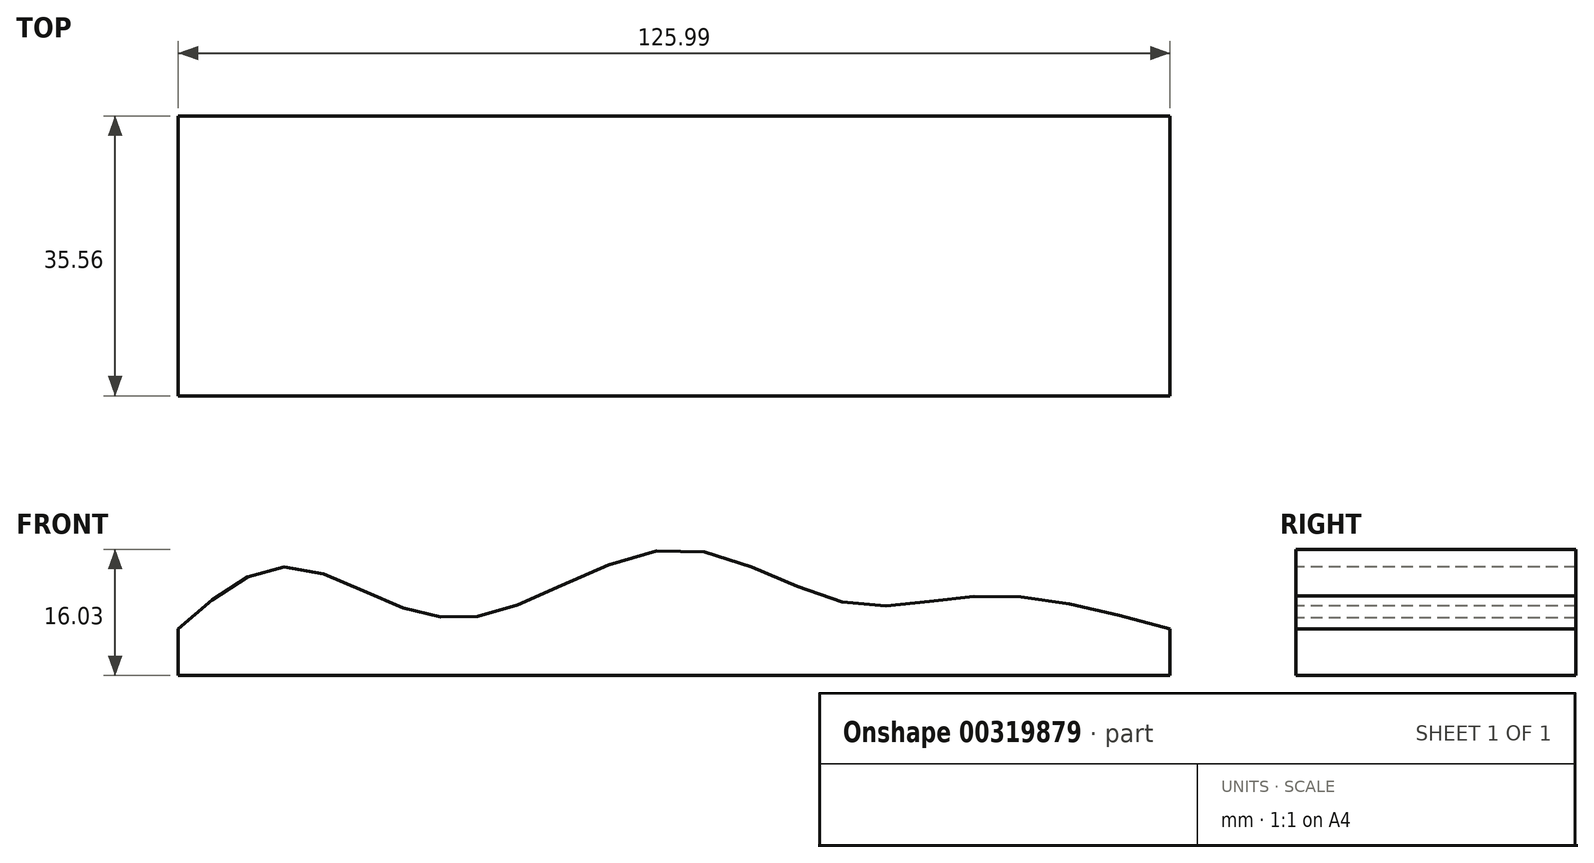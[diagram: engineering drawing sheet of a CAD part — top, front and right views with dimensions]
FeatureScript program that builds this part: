
annotation { "Feature Type Name" : "Feature", "Feature Type Description" : "" }
export const myFeature = defineFeature(function(context is Context, id is Id, definition is map)
    precondition{}
    {
        {
            var Q0;
            Q0=qCreatedBy(makeId("Front.planeOp"),FACE);
            var sketch = newSketch(context, id + "F0", { "sketchPlane" : qUnion([Q0])});
            skLineSegment(sketch, "E0.bottom", {"start": v(-134.15, -27.42) * mm, "end": v(-8.16, -27.42) * mm});
            skLineSegment(sketch, "E0.top", {"start": v(-134.15, -21.51) * mm, "end": v(-8.16, -21.51) * mm});
            skLineSegment(sketch, "E0.left", {"start": v(-134.15, -27.42) * mm, "end": v(-134.15, -21.51) * mm});
            skLineSegment(sketch, "E0.right", {"start": v(-8.16, -27.42) * mm, "end": v(-8.16, -21.51) * mm});
            skFitSpline(sketch, "E1", {"points": [v(-134.15, -21.51) * mm, v(-120.65, -13.64) * mm, v(-105.18, -18.98) * mm, v(-91.68, -18.7) * mm, v(-70.3, -11.39) * mm, v(-49.5, -18.14) * mm, v(-31.22, -17.3) * mm, v(-8.16, -21.51) * mm], "startDerivative": vector(99.16, 88.66) * mm, "endDerivative": vector(148.33, -40.96) * mm});
            skSolve(sketch);
        }
        {
            var Q0;
            Q0 = qSketchRegion(id + "F0", true);
            extrude(context, id + "F1", {"entities" : qUnion([Q0]), "depth" : 17.78 * mm});
        }
        {
            var Q0;
            Q0=makeQuery(id+"F1.opExtrude","SWEPT_BODY",BODY,{"disambiguationData":[OSD([sQuery(id+"F0.wireOp",EDGE,"E0.bottom"),sQuery(id+"F0.wireOp",EDGE,"E0.left"),sQuery(id+"F0.wireOp",EDGE,"E0.right"),sQuery(id+"F0.wireOp",EDGE,"E1")])]});
            var Q1;
            Q1=makeQuery(id+"F1.opExtrude","CAP_FACE",FACE,{"disambiguationData":[OSD([sQuery(id+"F0.wireOp",EDGE,"E0.bottom"),sQuery(id+"F0.wireOp",EDGE,"E0.left"),sQuery(id+"F0.wireOp",EDGE,"E0.right"),sQuery(id+"F0.wireOp",EDGE,"E1")])],"isStart":false});
            mirror(context, id + "F2", {"operationType" : NewBodyOperationType.ADD, "entities" : qUnion([Q0]), "mirrorPlane" : qUnion([Q1])});
        }
    });
